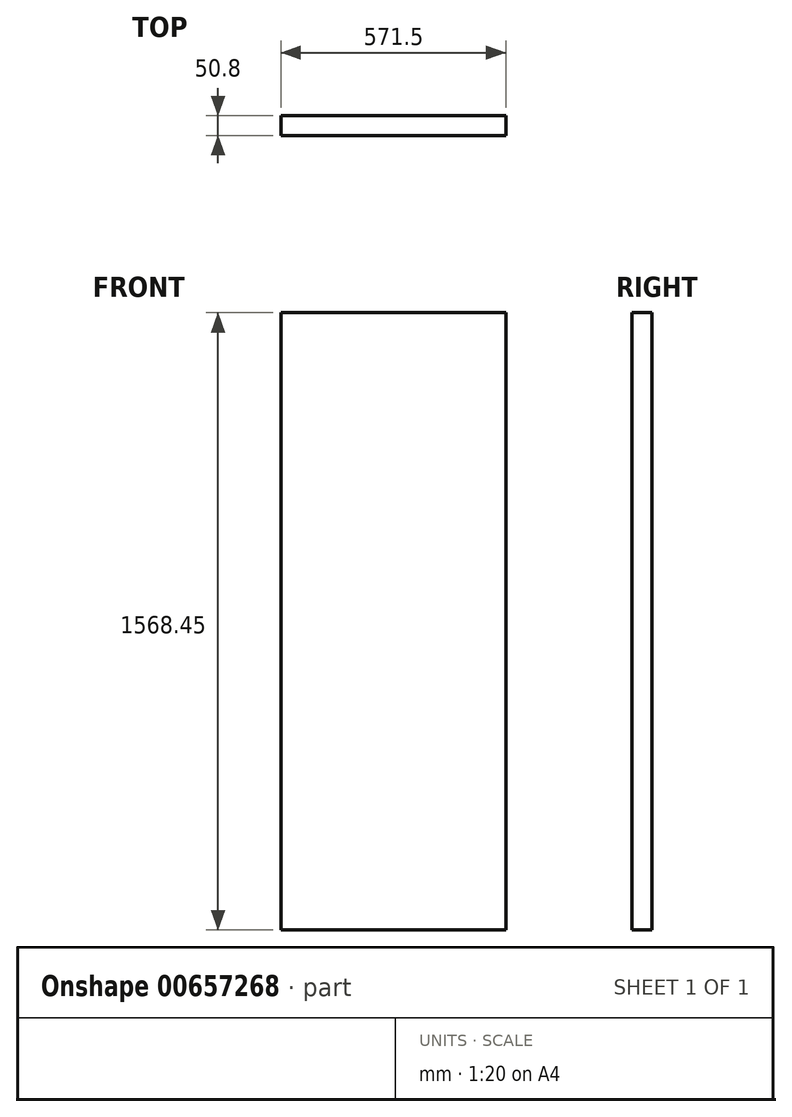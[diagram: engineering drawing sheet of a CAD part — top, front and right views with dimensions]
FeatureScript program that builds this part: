
annotation { "Feature Type Name" : "Feature", "Feature Type Description" : "" }
export const myFeature = defineFeature(function(context is Context, id is Id, definition is map)
    precondition{}
    {
        {
            var Q0;
            Q0=qCreatedBy(makeId("Front.planeOp"),FACE);
            var sketch = newSketch(context, id + "F0", { "sketchPlane" : qUnion([Q0])});
            skLineSegment(sketch, "E0.bottom", {"start": v(-279.4, 781.05) * mm, "end": v(292.1, 781.05) * mm});
            skLineSegment(sketch, "E0.top", {"start": v(-279.4, -787.4) * mm, "end": v(292.1, -787.4) * mm});
            skLineSegment(sketch, "E0.left", {"start": v(-279.4, 781.05) * mm, "end": v(-279.4, -787.4) * mm});
            skLineSegment(sketch, "E0.right", {"start": v(292.1, 781.05) * mm, "end": v(292.1, -787.4) * mm});
            skSolve(sketch);
        }
        {
            var Q0;
            Q0=qSketchRegion(id+"F0",true);
            extrude(context, id + "F1", {"entities" : qUnion([Q0]), "depth" : 50.8 * mm, "offsetDistance" : 25.4 * mm});
        }
    });
